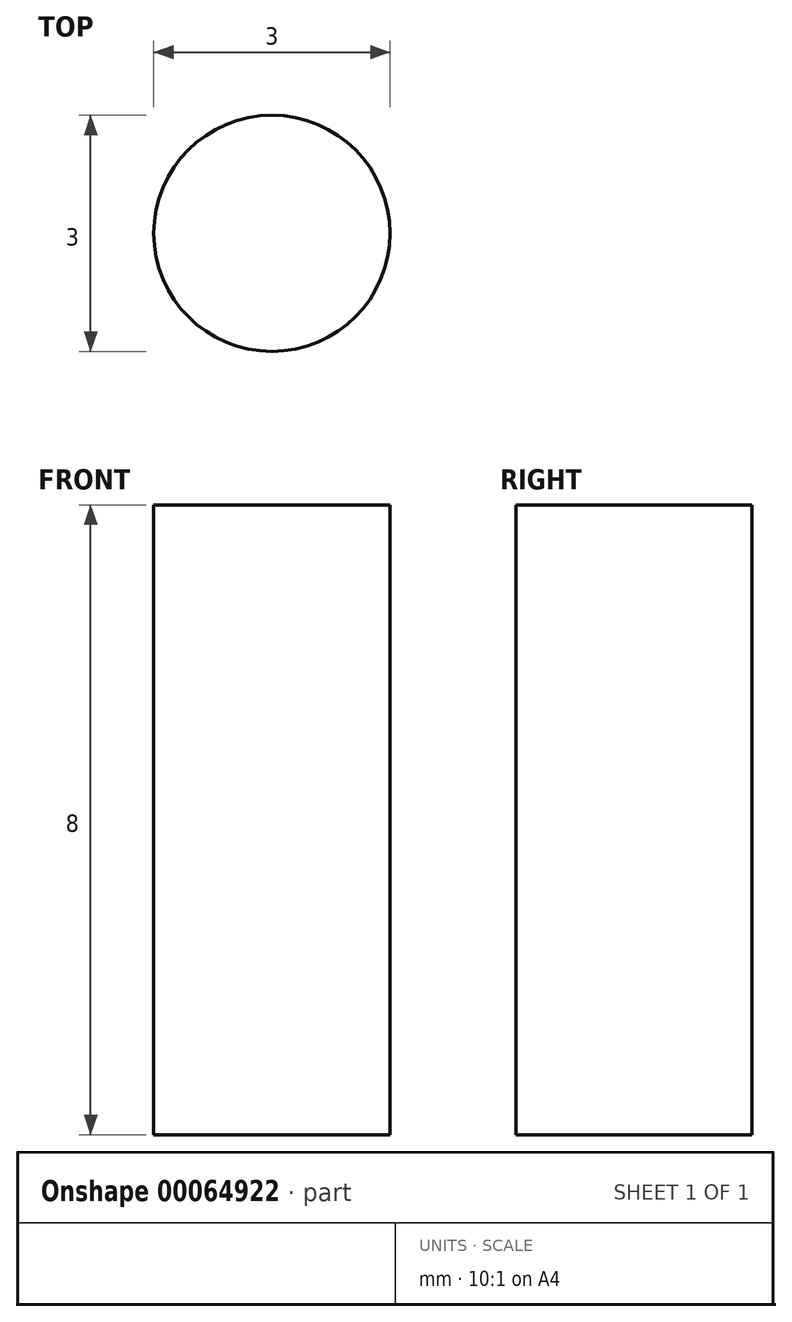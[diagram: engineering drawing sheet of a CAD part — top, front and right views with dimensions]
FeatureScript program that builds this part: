
annotation { "Feature Type Name" : "Feature", "Feature Type Description" : "" }
export const myFeature = defineFeature(function(context is Context, id is Id, definition is map)
    precondition{}
    {
        {
            var Q0;
            Q0=qCreatedBy(makeId("Top.planeOp"),FACE);
            var sketch = newSketch(context, id + "F0", { "sketchPlane" : qUnion([Q0])});
            skCircle(sketch, "E0", {"center": v(0, 0) * mm, "radius": 1.5 * mm});
            skSolve(sketch);
        }
        {
            var Q0;
            Q0 = qSketchRegion(id + "F0", true);
            extrude(context, id + "F1", {"entities" : qUnion([Q0]), "depth" : 8 * mm});
        }
    });
